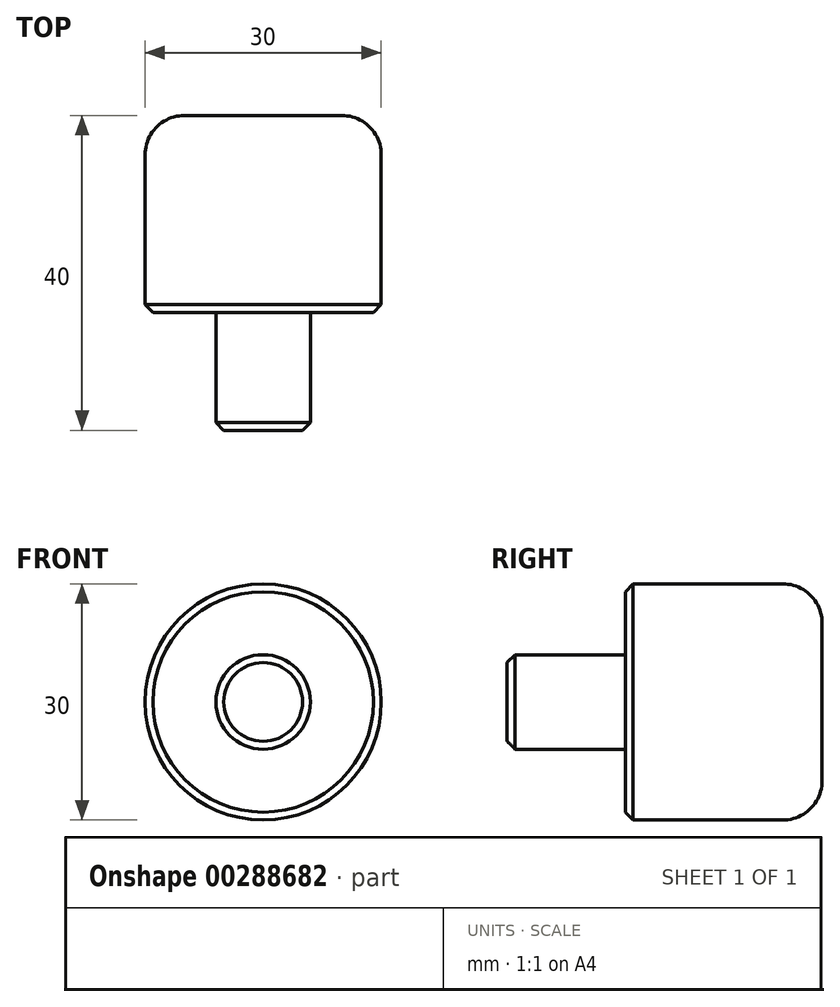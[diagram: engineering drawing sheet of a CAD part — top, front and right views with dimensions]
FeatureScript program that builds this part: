
annotation { "Feature Type Name" : "Feature", "Feature Type Description" : "" }
export const myFeature = defineFeature(function(context is Context, id is Id, definition is map)
    precondition{}
    {
        {
            var Q0;
            Q0=qCreatedBy(makeId("Front.planeOp"),FACE);
            var sketch = newSketch(context, id + "F0", { "sketchPlane" : qUnion([Q0])});
            skCircle(sketch, "E0", {"center": v(0, 0) * mm, "radius": 15 * mm});
            skSolve(sketch);
        }
        {
            var Q0;
            Q0=makeQuery(id+"F0.imprint","IMPRINT",FACE,{"disambiguationData":[TD([[makeQuery(id+"F0.imprint","IMPRINT",EDGE,{"derivedFrom":sQuery(id+"F0.wireOp",EDGE,"E0")}),1.0]])]});
            extrude(context, id + "F1", {"entities" : qUnion([Q0]), "depth" : 25 * mm});
        }
        {
            var Q0;
            Q0=makeQuery(id+"F1.opExtrude","CAP_FACE",FACE,{"disambiguationData":[OSD([sQuery(id+"F0.wireOp",EDGE,"E0")])],"isStart":false});
            var sketch = newSketch(context, id + "F2", { "sketchPlane" : qUnion([Q0])});
            skCircle(sketch, "E1", {"center": v(0, 0) * mm, "radius": 6 * mm});
            skSolve(sketch);
        }
        {
            var Q0;
            Q0=makeQuery(id+"F2.imprint","IMPRINT",FACE,{"disambiguationData":[TD([[makeQuery(id+"F2.imprint","IMPRINT",EDGE,{"derivedFrom":sQuery(id+"F2.wireOp",EDGE,"E1")}),1.0]])]});
            extrude(context, id + "F3", {"entities" : qUnion([Q0]), "operationType" : NewBodyOperationType.ADD, "depth" : 15 * mm});
        }
        {
            var Q0;
            Q0=makeQuery(id+"F1.opExtrude","CAP_EDGE",EDGE,{"disambiguationData":[OSD([sQuery(id+"F0.wireOp",EDGE,"E0")])],"isStart":true});
            fillet(context, id + "F4", {"entities" : qUnion([Q0]), "radius" : 5 * mm, "tangentPropagation" : true, "allowEdgeOverflow" : false});
        }
        {
            var Q0;
            Q0=makeQuery(id+"F3.opExtrude","CAP_EDGE",EDGE,{"disambiguationData":[OSD([sQuery(id+"F2.wireOp",EDGE,"E1")])],"isStart":false});
            var Q1;
            Q1=makeQuery(id+"F3.opExtrude","CAP_EDGE",EDGE,{"disambiguationData":[OSD([sQuery(id+"F2.wireOp",EDGE,"E1")])],"isStart":true});
            var Q2;
            Q2=makeQuery(id+"F1.opExtrude","CAP_EDGE",EDGE,{"disambiguationData":[OSD([sQuery(id+"F0.wireOp",EDGE,"E0")])],"isStart":false});
            chamfer(context, id + "F5", {"entities" : qUnion([Q0, Q1, Q2]), "width" : 1 * mm, "tangentPropagation" : true});
        }
    });
